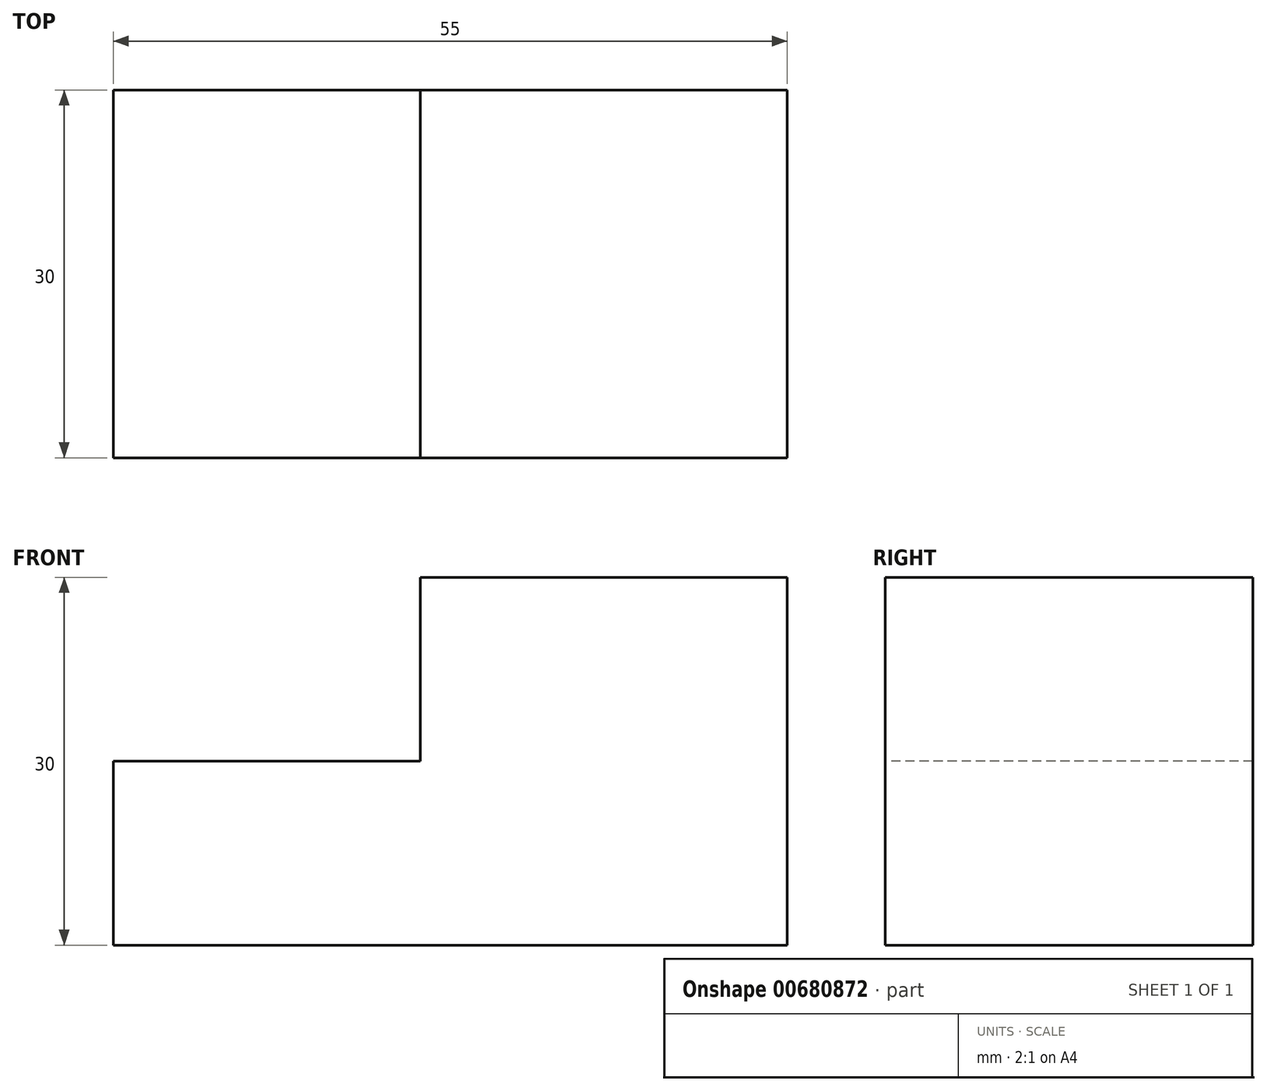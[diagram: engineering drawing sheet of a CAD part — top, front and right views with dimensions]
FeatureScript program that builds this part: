
annotation { "Feature Type Name" : "Feature", "Feature Type Description" : "" }
export const myFeature = defineFeature(function(context is Context, id is Id, definition is map)
    precondition{}
    {
        {
            var Q0;
            Q0=qCreatedBy(makeId("Top.planeOp"),FACE);
            var sketch = newSketch(context, id + "F0", { "sketchPlane" : qUnion([Q0])});
            skLineSegment(sketch, "E0.bottom", {"start": v(-27.5, 15) * mm, "end": v(27.5, 15) * mm});
            skLineSegment(sketch, "E0.top", {"start": v(-27.5, -15) * mm, "end": v(27.5, -15) * mm});
            skLineSegment(sketch, "E0.left", {"start": v(-27.5, 15) * mm, "end": v(-27.5, -15) * mm});
            skLineSegment(sketch, "E0.right", {"start": v(27.5, 15) * mm, "end": v(27.5, -15) * mm});
            skPoint(sketch, "E0.middle", {"position": v(0, 0) * mm});
            skSolve(sketch);
        }
        {
            var Q0;
            Q0=makeQuery(id+"F0.imprint","IMPRINT",FACE,{"disambiguationData":[TD([[makeQuery(id+"F0.imprint","IMPRINT",EDGE,{"derivedFrom":sQuery(id+"F0.wireOp",EDGE,"E0.bottom")}),-1.0]])]});
            extrude(context, id + "F1", {"entities" : qUnion([Q0]), "depth" : 30 * mm, "offsetDistance" : 25 * mm});
        }
        {
            var Q0;
            Q0=makeQuery(id+"F1.opExtrude","SWEPT_FACE",FACE,{"disambiguationData":[OSD([sQuery(id+"F0.wireOp",EDGE,"E0.top")])]});
            var sketch = newSketch(context, id + "F2", { "sketchPlane" : qUnion([Q0])});
            skLineSegment(sketch, "E1", {"start": v(-27.5, 15) * mm, "end": v(-2.45, 15) * mm});
            skLineSegment(sketch, "E2", {"start": v(-2.45, 15) * mm, "end": v(-2.45, 30) * mm});
            skSolve(sketch);
        }
        {
            var Q0;
            Q0=qSketchRegion(id+"F2",true);
            var Q1;
            {var subQ0=sQuery(id+"F2.wireOp",EDGE,"E1");Q1=makeQuery(id+"F2.imprint","IMPRINT",FACE,{"disambiguationData":[TD([[makeQuery(id+"F2.imprint","IMPRINT",EDGE,{"derivedFrom":subQ0}),1.0]])]});}
            extrude(context, id + "F3", {"entities" : qUnion([Q0, Q1]), "operationType" : NewBodyOperationType.REMOVE, "endBound" : BoundingType.THROUGH_ALL, "oppositeDirection" : true, "depth" : 25 * mm, "offsetDistance" : 25 * mm});
        }
    });
